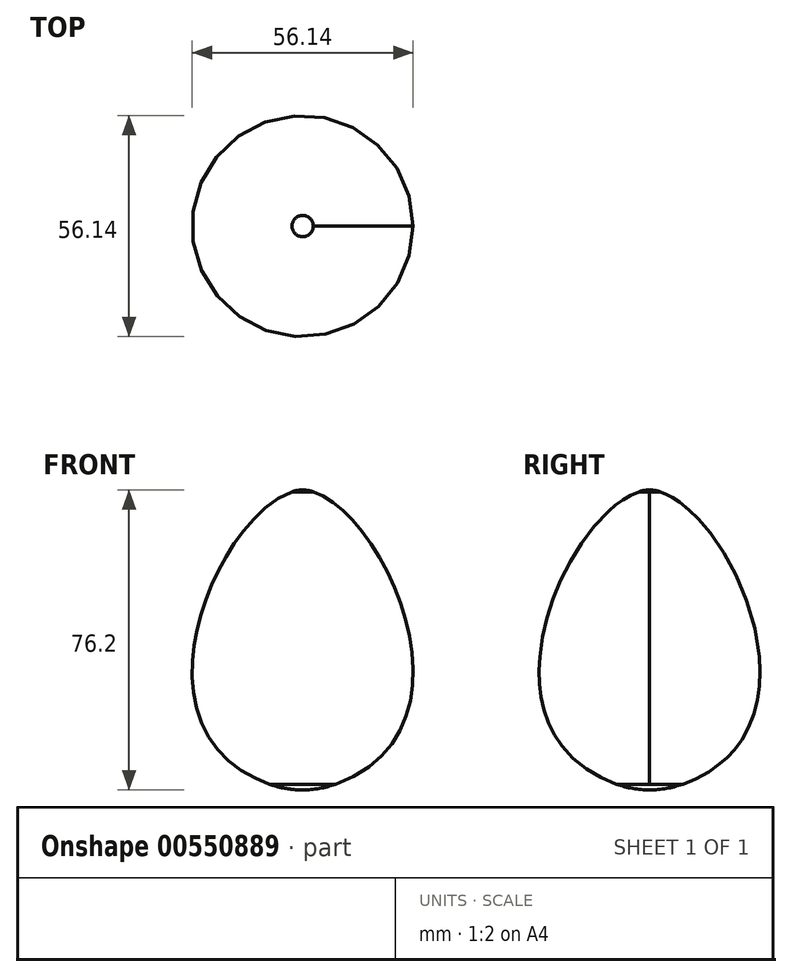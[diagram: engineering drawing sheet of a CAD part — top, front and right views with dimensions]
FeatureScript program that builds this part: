
annotation { "Feature Type Name" : "Feature", "Feature Type Description" : "" }
export const myFeature = defineFeature(function(context is Context, id is Id, definition is map)
    precondition{}
    {
        {
            var Q0;
            Q0=qCreatedBy(makeId("Front.planeOp"),FACE);
            var sketch = newSketch(context, id + "F0", { "sketchPlane" : qUnion([Q0])});
            skLineSegment(sketch, "E0", {"start": v(0, 38.1) * mm, "end": v(0, -38.1) * mm});
            skPoint(sketch, "E1.second.point", {"position": v(0, 11.9) * mm});
            skPoint(sketch, "E1.third.point", {"position": v(-24.5, -18.05) * mm});
            skPoint(sketch, "E2.second.point", {"position": v(0, 21.1) * mm});
            skPoint(sketch, "E2.third.point", {"position": v(-7.6, 25.78) * mm});
            skFitSpline(sketch, "E3", {"points": [v(8.41, -36.64) * mm, v(2.7, 37.66) * mm], "startDerivative": vector(112.32, 40.14) * mm, "endDerivative": vector(-56.89, 19.11) * mm});
            skFitSpline(sketch, "E4.MirrorCS", {"points": [v(-8.41, -36.64) * mm, v(-2.7, 37.66) * mm], "startDerivative": vector(-112.32, 40.14) * mm, "endDerivative": vector(56.89, 19.11) * mm});
            skLineSegment(sketch, "E5", {"start": v(-57.5, 0) * mm, "end": v(57.5, 0) * mm, "construction": true});
            skArc(sketch, "E6", {"start": v(0, 21.1) * mm, "mid": v(8.5, 29.6) * mm, "end": v(0, 38.1) * mm});
            skArc(sketch, "E7", {"start": v(0, 38.1) * mm, "mid": v(-8.5, 29.6) * mm, "end": v(0, 21.1) * mm});
            skArc(sketch, "E8", {"start": v(0, 11.9) * mm, "mid": v(-25, -13.1) * mm, "end": v(0, -38.1) * mm});
            skArc(sketch, "E9", {"start": v(0, -38.1) * mm, "mid": v(25, -13.1) * mm, "end": v(0, 11.9) * mm});
            skSolve(sketch);
        }
        {
            var Q0;
            {var subQ1=sQuery(id+"F0.wireOp",EDGE,"E6");var subQ5=makeQuery(id+"F0.imprint","INTERSECT",VERTEX,{"derivedFrom":[sQuery(id+"F0.wireOp",EDGE,"E3"),subQ1]});Q0=makeQuery(id+"F0.imprint","IMPRINT",FACE,{"disambiguationData":[TD([[makeQuery(id+"F0.imprint","IMPRINT",EDGE,{"disambiguationData":[TD([[subQ5,1.0]])],"derivedFrom":subQ1}),1.0]])]});}
            var Q1;
            {var subQ5=sQuery(id+"F0.wireOp",EDGE,"E3");Q1=makeQuery(id+"F0.imprint","IMPRINT",FACE,{"disambiguationData":[TD([[makeQuery(id+"F0.imprint","IMPRINT",EDGE,{"derivedFrom":subQ5}),1.0]])]});}
            var Q2;
            {var subQ0=sQuery(id+"F0.wireOp",EDGE,"E9");var subQ5=makeQuery(id+"F0.imprint","INTERSECT",VERTEX,{"derivedFrom":[sQuery(id+"F0.wireOp",EDGE,"E3"),subQ0]});Q2=makeQuery(id+"F0.imprint","IMPRINT",FACE,{"disambiguationData":[TD([[makeQuery(id+"F0.imprint","IMPRINT",EDGE,{"disambiguationData":[TD([[subQ5,1.0]])],"derivedFrom":subQ0}),1.0]])]});}
            var Q3;
            Q3=sQuery(id+"F0.wireOp",EDGE,"E0");
            revolve(context, id + "F1", {"entities" : qUnion([Q0, Q1, Q2]), "axis" : qUnion([Q3]), "revolveType" : RevolveType.FULL});
        }
    });
